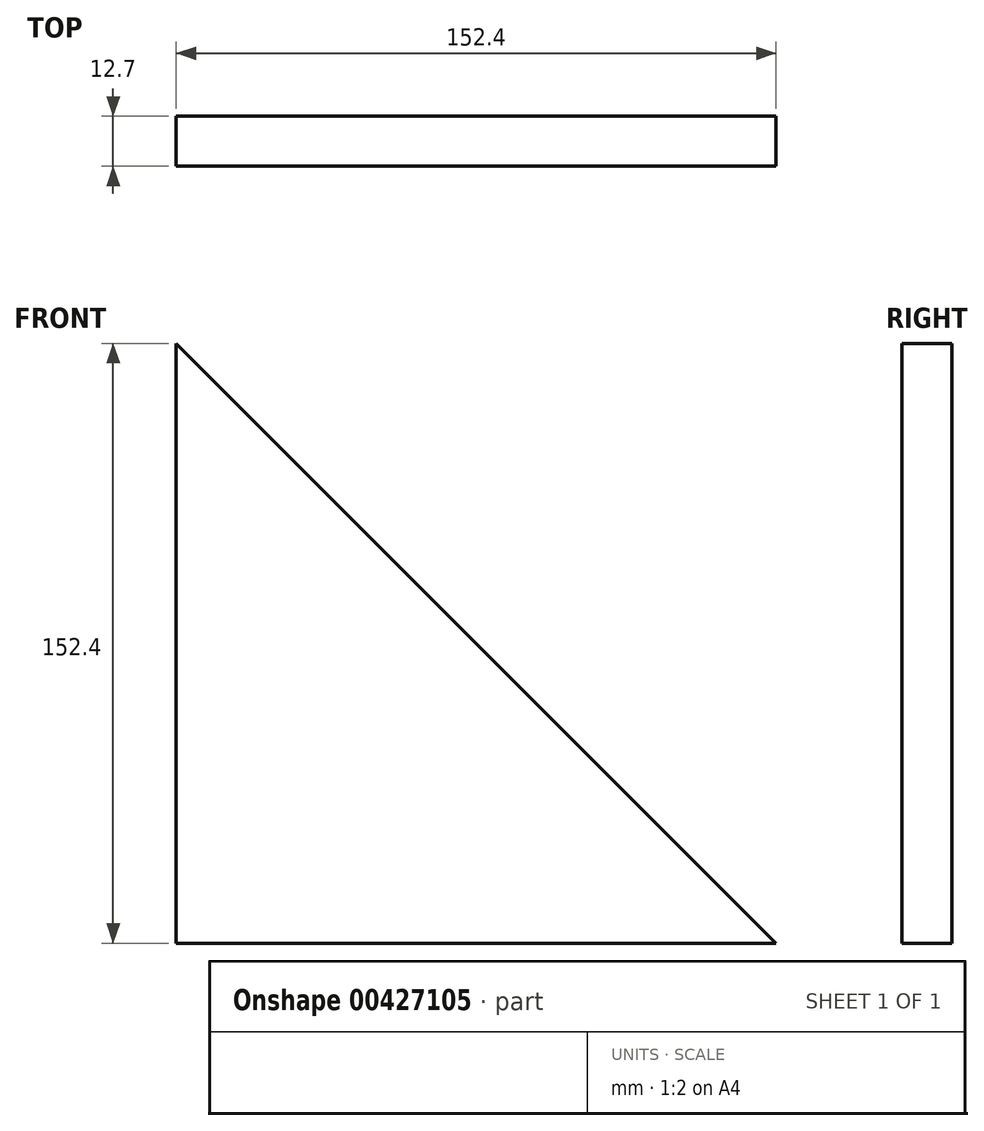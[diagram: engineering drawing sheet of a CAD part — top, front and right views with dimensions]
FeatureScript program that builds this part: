
annotation { "Feature Type Name" : "Feature", "Feature Type Description" : "" }
export const myFeature = defineFeature(function(context is Context, id is Id, definition is map)
    precondition{}
    {
        {
            var Q0;
            Q0=qCreatedBy(makeId("Front.planeOp"),FACE);
            var sketch = newSketch(context, id + "F0", { "sketchPlane" : qUnion([Q0])});
            skLineSegment(sketch, "E0", {"start": v(0, 152.15) * mm, "end": v(0, -0.25) * mm});
            skLineSegment(sketch, "E1", {"start": v(0, -0.25) * mm, "end": v(152.4, -0.25) * mm});
            skLineSegment(sketch, "E2", {"start": v(152.4, -0.25) * mm, "end": v(0, 152.15) * mm});
            skSolve(sketch);
        }
        {
            var Q0;
            Q0=makeQuery(id+"F0.imprint","IMPRINT",FACE,{"disambiguationData":[TD([[makeQuery(id+"F0.imprint","IMPRINT",EDGE,{"derivedFrom":sQuery(id+"F0.wireOp",EDGE,"E0")}),1.0]])]});
            extrude(context, id + "F1", {"entities" : qUnion([Q0]), "depth" : 12.7 * mm});
        }
    });
